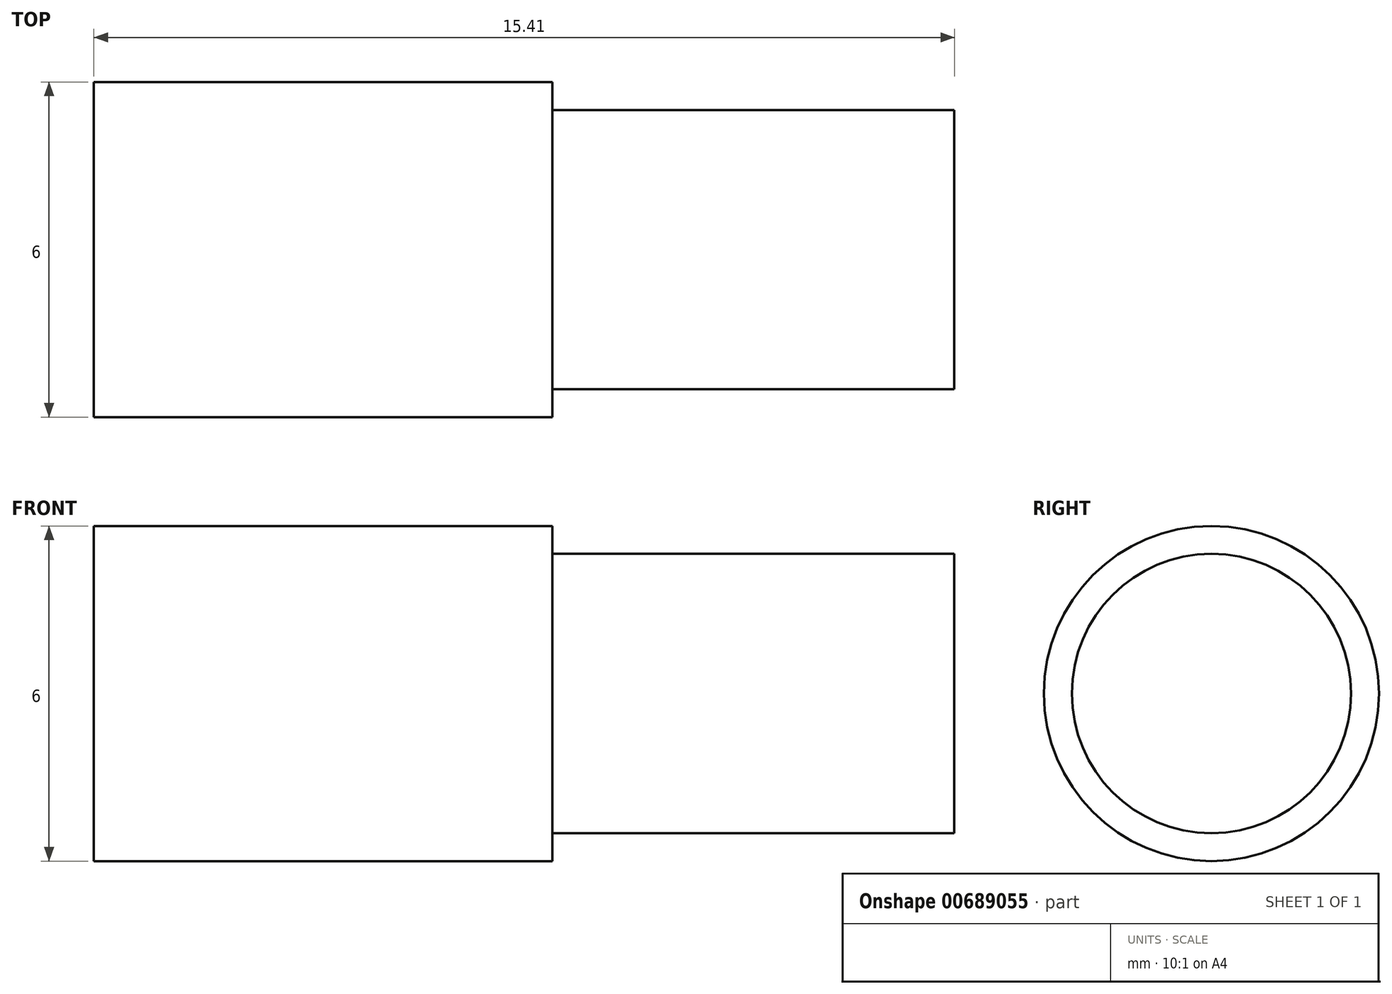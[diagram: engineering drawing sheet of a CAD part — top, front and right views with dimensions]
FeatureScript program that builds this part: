
annotation { "Feature Type Name" : "Feature", "Feature Type Description" : "" }
export const myFeature = defineFeature(function(context is Context, id is Id, definition is map)
    precondition{}
    {
        {
            var Q0;
            Q0=qCreatedBy(makeId("Top.planeOp"),FACE);
            var sketch = newSketch(context, id + "F0", { "sketchPlane" : qUnion([Q0])});
            skLineSegment(sketch, "E0.bottom", {"start": v(0, 0) * mm, "end": v(8.21, 0) * mm});
            skLineSegment(sketch, "E0.top", {"start": v(0, 3) * mm, "end": v(8.21, 3) * mm});
            skLineSegment(sketch, "E0.left", {"start": v(0, 0) * mm, "end": v(0, 3) * mm});
            skLineSegment(sketch, "E0.right", {"start": v(8.21, 0) * mm, "end": v(8.21, 3) * mm});
            skLineSegment(sketch, "E1.bottom", {"start": v(8.21, 0) * mm, "end": v(15.4, 0) * mm});
            skLineSegment(sketch, "E1.top", {"start": v(8.21, 2.5) * mm, "end": v(15.4, 2.5) * mm});
            skLineSegment(sketch, "E1.left", {"start": v(8.21, 0) * mm, "end": v(8.21, 2.5) * mm});
            skLineSegment(sketch, "E1.right", {"start": v(15.4, 0) * mm, "end": v(15.4, 2.5) * mm});
            skSolve(sketch);
        }
        {
            var Q0;
            Q0=makeQuery(id+"F0.imprint","IMPRINT",FACE,{"disambiguationData":[TD([[makeQuery(id+"F0.imprint","IMPRINT",EDGE,{"derivedFrom":sQuery(id+"F0.wireOp",EDGE,"E0.bottom")}),1.0]])]});
            var Q1;
            Q1=makeQuery(id+"F0.imprint","IMPRINT",FACE,{"disambiguationData":[TD([[makeQuery(id+"F0.imprint","IMPRINT",EDGE,{"derivedFrom":sQuery(id+"F0.wireOp",EDGE,"E1.bottom")}),1.0]])]});
            var Q2;
            Q2=sQuery(id+"F0.wireOp",EDGE,"E0.bottom");
            revolve(context, id + "F1", {"surfaceOperationType" : NewSurfaceOperationType.NEW, "entities" : qUnion([Q0, Q1]), "axis" : qUnion([Q2]), "revolveType" : RevolveType.FULL});
        }
    });
